# Revit family: Seating-Casual-Naughtone-Fold_Bench
name_source: partatom
category: Furniture
revit_build: Autodesk Revit 2015 (Build: 20150704_0715(x64)
units: mm (PartAtom-declared; Revit-internal decimal feet)

## types (3) — shared parameters
AdditionalMaterials = Additional material and finish options available. Please contact Naughtone direct for further information.
Assembly Code = E2020
AssetType = Movable
BIMObjectName = Seating-Casual-Naughtone-Fold_Bench
BarCode = 0.000000
Category = 40.50.12.21 : Dining Benches
CodePerformance = FISP Certified; ISO14001 Certified
Color = White
ComponentDescription = Strong and elegant, fold tables and benches proovide a simple surface with maximum clearance for legs, chairs and fresh air to fit underneath!
Constituents = Wood Top; Steel frame
Description = Fold Bench
DurationUnit = Years
ExpectedLife = 15-20
Finish = Polyster powder coat; various top finishes available
Keynote = 40.50.12.21
Manufacturer = Naughtone
ManufacturerAddressUK = 201 Pannal Business Park, Station Road, Harrogate, HG3 1JL
Material = Timber; folded mild steel frame
ModelReference = Fold Bench
NBSReference = 40.50.12.21
NominalHeight = 450 mm  [stored 1.47638 ft]
NominalLength = 275 mm
Product URL = http://www.naughtone.com
ProductInformation = http://www.naughtone.com
ReplacementCost = 0.00
SerialNumber = 0.000000
Shape = Rectangular
SustainabilityPerformance = 55.3% reusable content. 72% recycled & recyclable content
TagNumber = 0.000000
TypeName = Seating-Casual-Naughtone-Fold_Bench
URL = http://www.naughtone.com
Uniclass2015 = 40.50.12.21
Version = 1
WarrantyDescription = 5 year warranty
WarrantyDurationLabor = 5
WarrantyDurationParts = 5
WarrantyDurationUnit = Years
_current revision = 1
_distributed by = www.bimbox.co.uk
zero-valued in all types: Cost, _BIMspec_GUID

## per-type parameters (varying)
| type | AssetIdentifier | Model | ModelNumber | Name | NominalWidth | Type Comments |
| 1650mmx275mmx450mm | FOLDBEN-1650 | FOLDBEN-1650 | FOLDBEN-1650 | 1650mmx275mmx450mm, Fold Bench | 1650 mm  [stored 5.41339 ft] | 1650x275x450 |
| 1250mmx275mmx450mm | FOLDBEN-1250 | FOLDBEN-1250 | FOLDBEN-1250 | 1250mmx275mmx450mm, Fold Bench | 1250 mm  [stored 4.10105 ft] | 1250x275x450 |
| 1450mmx275mmx450mm | FOLDBEN-1450 | FOLDBEN-1450 | FOLDBEN-1450 | 1450mmx275mmx450mm, Fold Bench | 1450 mm  [stored 4.75722 ft] | 1450x275x450 |

note: column(s) folded — value = type name in every type: Size

note: [stored X ft] marks values corroborated as IEEE doubles in the binary element streams (Revit-internal decimal feet)

## geometry (parser evidence)
native form markers: Sweep x5
no freeform markers — native parametric forms only
